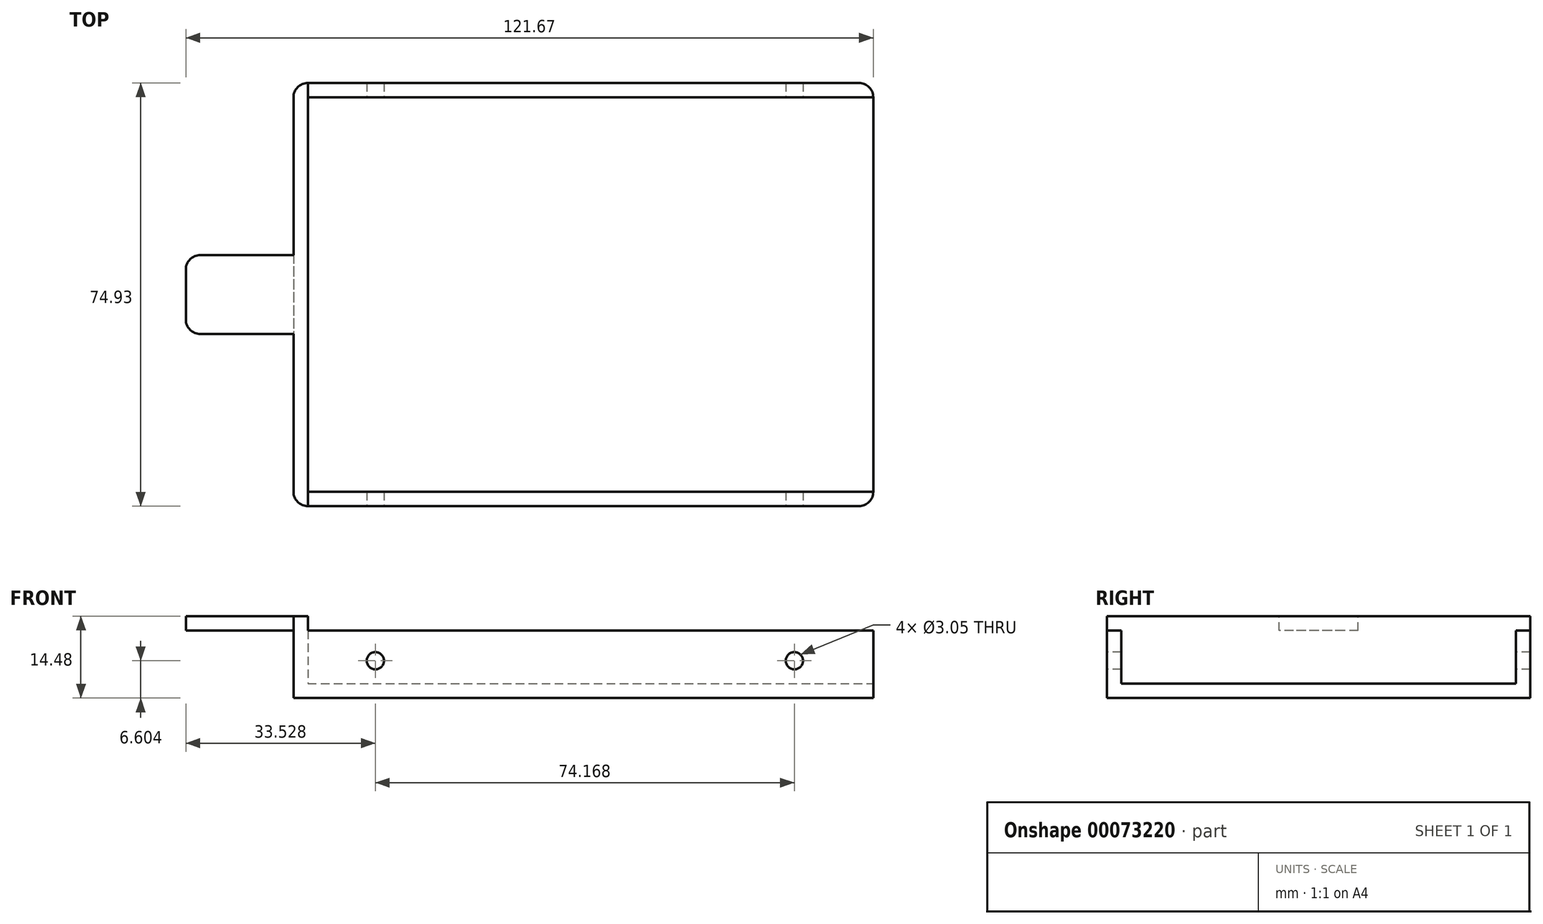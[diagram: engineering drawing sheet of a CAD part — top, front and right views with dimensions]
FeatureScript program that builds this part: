
annotation { "Feature Type Name" : "Feature", "Feature Type Description" : "" }
export const myFeature = defineFeature(function(context is Context, id is Id, definition is map)
    precondition{}
    {
        {
            var Q0;
            Q0=qCreatedBy(makeId("Top.planeOp"),FACE);
            var sketch = newSketch(context, id + "F0", { "sketchPlane" : qUnion([Q0])});
            skLineSegment(sketch, "E0.bottom", {"start": v(0, 0) * mm, "end": v(100.08, 0) * mm});
            skLineSegment(sketch, "E0.top", {"start": v(0, 69.85) * mm, "end": v(100.08, 69.85) * mm});
            skLineSegment(sketch, "E0.left", {"start": v(0, 0) * mm, "end": v(0, 69.85) * mm});
            skLineSegment(sketch, "E0.right", {"start": v(100.08, 0) * mm, "end": v(100.08, 69.85) * mm});
            skLineSegment(sketch, "E1.top", {"start": v(0, 72.4) * mm, "end": v(100.08, 72.4) * mm});
            skLineSegment(sketch, "E1.left", {"start": v(0, 69.85) * mm, "end": v(0, 72.4) * mm});
            skLineSegment(sketch, "E1.right", {"start": v(100.08, 69.85) * mm, "end": v(100.08, 72.4) * mm});
            skLineSegment(sketch, "E2.top", {"start": v(0, -2.54) * mm, "end": v(100.08, -2.54) * mm});
            skLineSegment(sketch, "E2.left", {"start": v(0, 0) * mm, "end": v(0, -2.54) * mm});
            skLineSegment(sketch, "E2.right", {"start": v(100.08, 0) * mm, "end": v(100.08, -2.54) * mm});
            skLineSegment(sketch, "E3.bottom", {"start": v(0, 72.4) * mm, "end": v(-2.54, 72.4) * mm});
            skLineSegment(sketch, "E3.top", {"start": v(0, -2.54) * mm, "end": v(-2.54, -2.54) * mm});
            skLineSegment(sketch, "E3.left", {"start": v(0, 72.4) * mm, "end": v(0, -2.54) * mm});
            skLineSegment(sketch, "E3.right", {"start": v(-2.54, 72.4) * mm, "end": v(-2.54, -2.54) * mm});
            skSolve(sketch);
        }
        {
            var Q0;
            {var subQ0=sQuery(id+"F0.wireOp",EDGE,"E0.top");Q0=makeQuery(id+"F0.imprint","IMPRINT",FACE,{"disambiguationData":[TD([[makeQuery(id+"F0.imprint","IMPRINT",EDGE,{"derivedFrom":subQ0}),1.0]])]});}
            var Q1;
            {var subQ0=sQuery(id+"F0.wireOp",EDGE,"E0.bottom");Q1=makeQuery(id+"F0.imprint","IMPRINT",FACE,{"disambiguationData":[TD([[makeQuery(id+"F0.imprint","IMPRINT",EDGE,{"derivedFrom":subQ0}),-1.0]])]});}
            extrude(context, id + "F1", {"entities" : qUnion([Q0, Q1]), "depth" : 11.94 * mm});
        }
        {
            var Q0;
            Q0=makeQuery(id+"F0.imprint","IMPRINT",FACE,{"disambiguationData":[TD([[makeQuery(id+"F0.imprint","IMPRINT",EDGE,{"derivedFrom":sQuery(id+"F0.wireOp",EDGE,"E0.right")}),1.0]])]});
            extrude(context, id + "F2", {"entities" : qUnion([Q0]), "operationType" : NewBodyOperationType.ADD, "depth" : 2.54 * mm});
        }
        {
            var Q0;
            Q0=makeQuery(id+"F1.opExtrude","SWEPT_FACE",FACE,{"disambiguationData":[OSD([sQuery(id+"F0.wireOp",EDGE,"E2.top"),sQuery(id+"F0.wireOp",EDGE,"E3.top")])]});
            var sketch = newSketch(context, id + "F3", { "sketchPlane" : qUnion([Q0])});
            skLineSegment(sketch, "E4", {"start": v(100.08, 6.6) * mm, "end": v(86.1, 6.6) * mm, "construction": true});
            skCircle(sketch, "E5", {"center": v(86.1, 6.6) * mm, "radius": 1.52 * mm});
            skLineSegment(sketch, "E6", {"start": v(86.1, 6.6) * mm, "end": v(86.1, 0) * mm, "construction": true});
            skLineSegment(sketch, "E7", {"start": v(0, 6.6) * mm, "end": v(11.94, 6.6) * mm, "construction": true});
            skLineSegment(sketch, "E8", {"start": v(11.94, 6.6) * mm, "end": v(11.94, 0) * mm, "construction": true});
            skCircle(sketch, "E9", {"center": v(11.94, 6.6) * mm, "radius": 1.52 * mm});
            skSolve(sketch);
        }
        {
            var Q0;
            {var subQ3=sQuery(id+"F0.wireOp",EDGE,"E3.bottom");Q0=makeQuery(id+"F0.imprint","IMPRINT",FACE,{"disambiguationData":[TD([[makeQuery(id+"F0.imprint","IMPRINT",EDGE,{"derivedFrom":subQ3}),1.0]])]});}
            extrude(context, id + "F4", {"entities" : qUnion([Q0]), "operationType" : NewBodyOperationType.ADD, "depth" : 14.48 * mm});
        }
        {
            var Q0;
            Q0=makeQuery(id+"F4.opExtrude","SWEPT_FACE",FACE,{"disambiguationData":[OSD([sQuery(id+"F0.wireOp",EDGE,"E3.right")])]});
            var sketch = newSketch(context, id + "F5", { "sketchPlane" : qUnion([Q0])});
            skLineSegment(sketch, "E10", {"start": v(2.54, 11.94) * mm, "end": v(-27.94, 11.94) * mm, "construction": true});
            skLineSegment(sketch, "E11", {"start": v(-72.4, 11.94) * mm, "end": v(-41.91, 11.94) * mm, "construction": true});
            skLineSegment(sketch, "E12.bottom", {"start": v(-41.91, 11.94) * mm, "end": v(-27.94, 11.94) * mm});
            skLineSegment(sketch, "E12.top", {"start": v(-41.91, 14.48) * mm, "end": v(-27.94, 14.48) * mm});
            skLineSegment(sketch, "E12.left", {"start": v(-41.91, 11.94) * mm, "end": v(-41.91, 14.48) * mm});
            skLineSegment(sketch, "E12.right", {"start": v(-27.94, 11.94) * mm, "end": v(-27.94, 14.48) * mm});
            skSolve(sketch);
        }
        {
            var Q0;
            Q0=makeQuery(id+"F5.imprint","IMPRINT",FACE,{"disambiguationData":[TD([[makeQuery(id+"F5.imprint","IMPRINT",EDGE,{"derivedFrom":sQuery(id+"F5.wireOp",EDGE,"E12.bottom")}),1.0]])]});
            extrude(context, id + "F6", {"entities" : qUnion([Q0]), "operationType" : NewBodyOperationType.ADD, "depth" : 19.05 * mm});
        }
        {
            var Q0;
            Q0=makeQuery(id+"F6.opExtrude","CAP_EDGE",EDGE,{"disambiguationData":[OSD([sQuery(id+"F5.wireOp",EDGE,"E12.right")])],"isStart":false});
            var Q1;
            Q1=makeQuery(id+"F6.opExtrude","CAP_EDGE",EDGE,{"disambiguationData":[OSD([sQuery(id+"F5.wireOp",EDGE,"E12.left")])],"isStart":false});
            var Q2;
            Q2=makeQuery(id+"F6.opExtrude","CAP_EDGE",EDGE,{"disambiguationData":[OSD([sQuery(id+"F5.wireOp",EDGE,"E12.left")])],"isStart":true});
            var Q3;
            Q3=makeQuery(id+"F6.opExtrude","CAP_EDGE",EDGE,{"disambiguationData":[OSD([sQuery(id+"F5.wireOp",EDGE,"E12.right")])],"isStart":true});
            var Q4;
            Q4=makeQuery(id+"F4.opExtrude","SWEPT_EDGE",EDGE,{"disambiguationData":[OSD([sQuery(id+"F0.wireOp",EDGE,"E3.top"),sQuery(id+"F0.wireOp",EDGE,"E3.right")])]});
            var Q5;
            Q5=makeQuery(id+"F1.opExtrude","SWEPT_EDGE",EDGE,{"disambiguationData":[OSD([sQuery(id+"F0.wireOp",EDGE,"E2.top"),sQuery(id+"F0.wireOp",EDGE,"E2.right")])]});
            var Q6;
            Q6=makeQuery(id+"F1.opExtrude","SWEPT_EDGE",EDGE,{"disambiguationData":[OSD([sQuery(id+"F0.wireOp",EDGE,"E1.top"),sQuery(id+"F0.wireOp",EDGE,"E1.right")])]});
            var Q7;
            Q7=makeQuery(id+"F4.opExtrude","SWEPT_EDGE",EDGE,{"disambiguationData":[OSD([sQuery(id+"F0.wireOp",EDGE,"E3.bottom"),sQuery(id+"F0.wireOp",EDGE,"E3.right")])]});
            var Q8;
            {var subQ0=sQuery(id+"F0.wireOp",EDGE,"E3.left");Q8=makeQuery(id+"F1.opExtrude","CAP_EDGE",EDGE,{"disambiguationData":[OSD([subQ0]),TDD([makeQuery(id+"F0.imprint","IMPRINT",EDGE,{"disambiguationData":[TD([[makeQuery(id+"F0.imprint","INTERSECT",VERTEX,{"derivedFrom":[sQuery(id+"F0.wireOp",EDGE,"E0.top"),subQ0]}),1.0]])],"derivedFrom":subQ0})])],"isStart":false});}
            var Q9;
            {var subQ0=sQuery(id+"F0.wireOp",EDGE,"E3.left");Q9=makeQuery(id+"F1.opExtrude","CAP_EDGE",EDGE,{"disambiguationData":[OSD([subQ0]),TDD([makeQuery(id+"F0.imprint","IMPRINT",EDGE,{"disambiguationData":[TD([[makeQuery(id+"F0.imprint","INTERSECT",VERTEX,{"derivedFrom":[sQuery(id+"F0.wireOp",EDGE,"E0.bottom"),subQ0]}),-1.0]])],"derivedFrom":subQ0})])],"isStart":false});}
            var Q10;
            Q10=makeQuery(id+"F6.opExtrude","CAP_EDGE",EDGE,{"disambiguationData":[OSD([sQuery(id+"F5.wireOp",EDGE,"E12.bottom")])],"isStart":true});
            fillet(context, id + "F7", {"entities" : qUnion([Q0, Q1, Q2, Q3, Q4, Q5, Q6, Q7, Q8, Q9, Q10]), "radius" : 2.54 * mm, "tangentPropagation" : true, "allowEdgeOverflow" : false});
        }
        {
            var Q0;
            Q0=makeQuery(id+"F3.imprint","IMPRINT",FACE,{"disambiguationData":[TD([[makeQuery(id+"F3.imprint","IMPRINT",EDGE,{"derivedFrom":sQuery(id+"F3.wireOp",EDGE,"E5")}),1.0]])]});
            var Q1;
            Q1=makeQuery(id+"F3.imprint","IMPRINT",FACE,{"disambiguationData":[TD([[makeQuery(id+"F3.imprint","IMPRINT",EDGE,{"derivedFrom":sQuery(id+"F3.wireOp",EDGE,"E9")}),1.0]])]});
            extrude(context, id + "F8", {"entities" : qUnion([Q0, Q1]), "operationType" : NewBodyOperationType.REMOVE, "oppositeDirection" : true, "depth" : 76.2 * mm});
        }
    });
